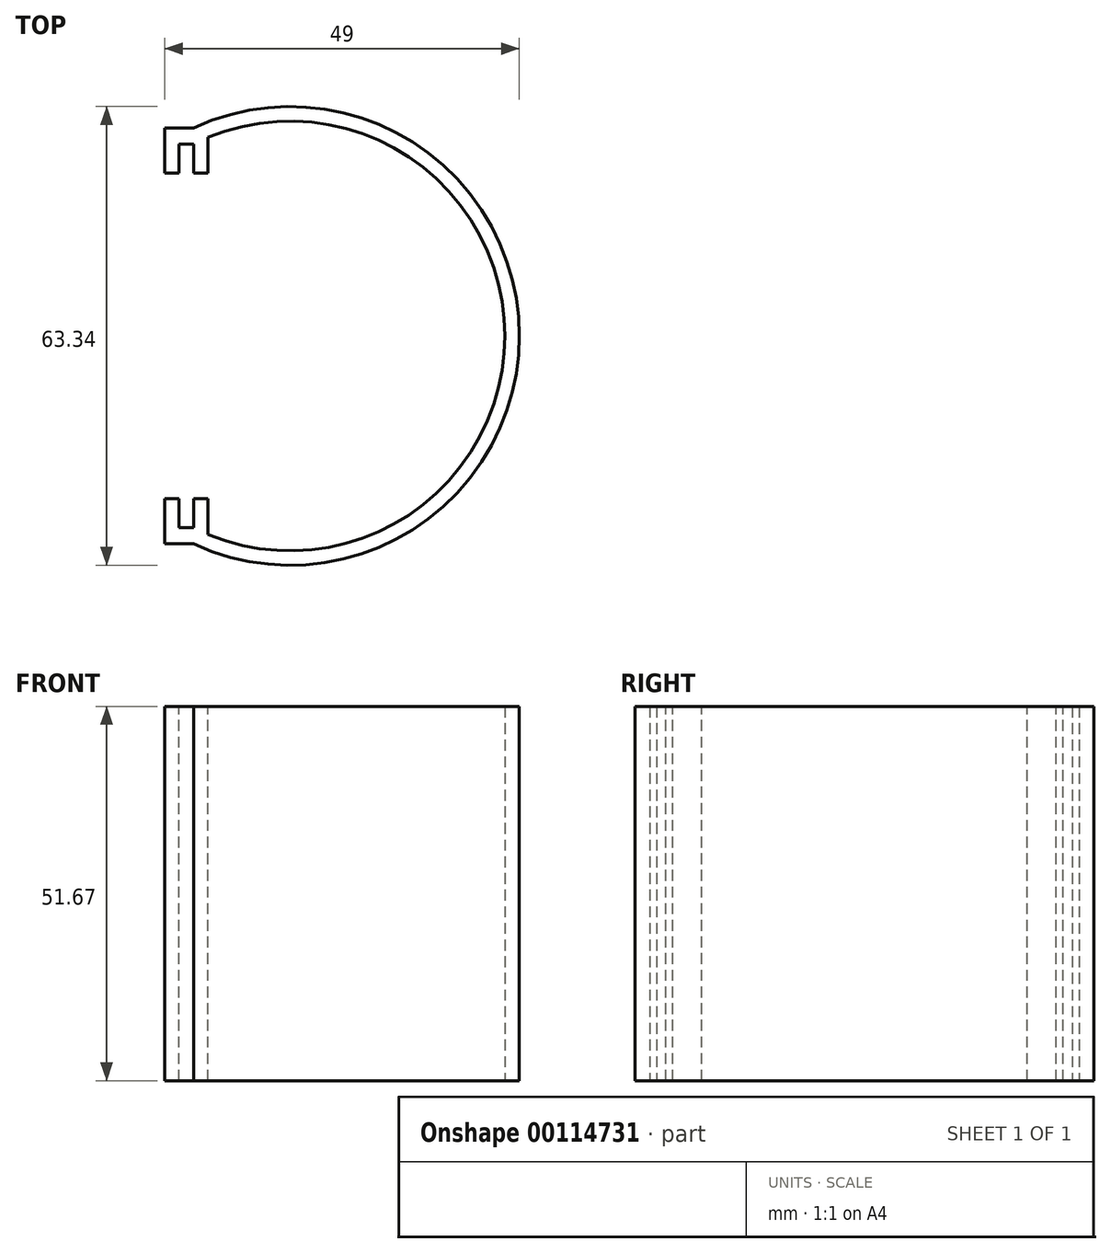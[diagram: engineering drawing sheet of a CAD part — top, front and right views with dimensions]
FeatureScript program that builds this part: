
annotation { "Feature Type Name" : "Feature", "Feature Type Description" : "" }
export const myFeature = defineFeature(function(context is Context, id is Id, definition is map)
    precondition{}
    {
        {
            var Q0;
            Q0=qCreatedBy(makeId("Top.planeOp"),FACE);
            var sketch = newSketch(context, id + "F0", { "sketchPlane" : qUnion([Q0])});
            skArc(sketch, "E0", {"start": v(-13.33, -26.5) * mm, "mid": v(29.67, 0) * mm, "end": v(-13.33, 26.5) * mm});
            skLineSegment(sketch, "E1", {"start": v(-13.33, -28.72) * mm, "end": v(-13.33, -26.5) * mm});
            skPoint(sketch, "E2", {"position": v(-13.33, 26.5) * mm});
            skPoint(sketch, "E3", {"position": v(-13.33, -26.5) * mm});
            skArc(sketch, "E4", {"start": v(-13.33, -28.72) * mm, "mid": v(31.67, 0) * mm, "end": v(-13.33, 28.72) * mm});
            skLineSegment(sketch, "E5.trimOffspring", {"start": v(-13.33, 26.5) * mm, "end": v(-13.33, 28.72) * mm});
            skPoint(sketch, "E6.start.orphan", {"position": v(-13.33, 0) * mm});
            skPoint(sketch, "E7.orphan", {"position": v(-13.33, 36.5) * mm});
            skPoint(sketch, "E8.orphan", {"position": v(-13.33, -36.5) * mm});
            skSolve(sketch);
        }
        {
            var Q0;
            Q0 = qSketchRegion(id + "F0", true);
            extrude(context, id + "F1", {"entities" : qUnion([Q0]), "depth" : 51.67 * mm});
        }
        {
            var Q0;
            Q0=makeQuery(id+"F1.opExtrude","CAP_FACE",FACE,{"disambiguationData":[OSD([sQuery(id+"F0.wireOp",EDGE,"E0"),sQuery(id+"F0.wireOp",EDGE,"E1"),sQuery(id+"F0.wireOp",EDGE,"E4"),sQuery(id+"F0.wireOp",EDGE,"E5.trimOffspring")])],"isStart":false});
            var sketch = newSketch(context, id + "F2", { "sketchPlane" : qUnion([Q0])});
            skLineSegment(sketch, "E9", {"start": v(-11.33, 27.42) * mm, "end": v(-11.33, 22.5) * mm});
            skLineSegment(sketch, "E10", {"start": v(-11.33, 22.5) * mm, "end": v(-13.33, 22.5) * mm});
            skLineSegment(sketch, "E11", {"start": v(-13.33, 22.5) * mm, "end": v(-13.33, 26.5) * mm});
            skLineSegment(sketch, "E12", {"start": v(-13.33, 26.5) * mm, "end": v(-15.33, 26.5) * mm});
            skLineSegment(sketch, "E13", {"start": v(-15.33, 26.5) * mm, "end": v(-15.33, 22.5) * mm});
            skLineSegment(sketch, "E14", {"start": v(-15.33, 22.5) * mm, "end": v(-17.33, 22.5) * mm});
            skLineSegment(sketch, "E15", {"start": v(-17.33, 22.5) * mm, "end": v(-17.33, 26.5) * mm});
            skLineSegment(sketch, "E16", {"start": v(-17.33, 26.5) * mm, "end": v(-17.33, 28.72) * mm});
            skLineSegment(sketch, "E17", {"start": v(-17.33, 28.72) * mm, "end": v(-13.33, 28.72) * mm});
            skSolve(sketch);
        }
        {
            var Q0;
            Q0=makeQuery(id+"F2.imprint","IMPRINT",FACE,{"disambiguationData":[TD([[makeQuery(id+"F2.imprint","IMPRINT",EDGE,{"derivedFrom":sQuery(id+"F2.wireOp",EDGE,"E12")}),-1.0]])]});
            var Q1;
            {var subQ0=sQuery(id+"F2.wireOp",EDGE,"E9");Q1=makeQuery(id+"F2.imprint","IMPRINT",FACE,{"disambiguationData":[TD([[makeQuery(id+"F2.imprint","IMPRINT",EDGE,{"derivedFrom":subQ0}),-1.0]])]});}
            extrude(context, id + "F3", {"entities" : qUnion([Q0, Q1]), "operationType" : NewBodyOperationType.ADD, "oppositeDirection" : true, "depth" : 51.67 * mm});
        }
        {
            var Q0;
            Q0=makeQuery(id+"F1.opExtrude","SWEPT_BODY",BODY,{"disambiguationData":[OSD([sQuery(id+"F0.wireOp",EDGE,"E0"),sQuery(id+"F0.wireOp",EDGE,"E1"),sQuery(id+"F0.wireOp",EDGE,"E4"),sQuery(id+"F0.wireOp",EDGE,"E5.trimOffspring")])]});
            var Q1;
            Q1=qCreatedBy(makeId("Front.planeOp"),FACE);
            mirror(context, id + "F4", {"operationType" : NewBodyOperationType.ADD, "entities" : qUnion([Q0]), "mirrorPlane" : qUnion([Q1])});
        }
        {
            var Q0;
            {var subQ0=sQuery(id+"F0.wireOp",EDGE,"E5.trimOffspring");var subQ1=sQuery(id+"F0.wireOp",EDGE,"E0");var subQ2=makeQuery(id+"F3.boolean.opBoolean","MERGE",FACE,{"derivedFrom":[makeQuery(id+"F1.opExtrude","CAP_FACE",FACE,{"disambiguationData":[OSD([subQ1,sQuery(id+"F0.wireOp",EDGE,"E1"),sQuery(id+"F0.wireOp",EDGE,"E4"),subQ0])],"isStart":false}),makeQuery(id+"F3.opExtrude","CAP_FACE",FACE,{"disambiguationData":[OSD([subQ1,sQuery(id+"F2.wireOp",EDGE,"E9"),sQuery(id+"F2.wireOp",EDGE,"E10"),sQuery(id+"F2.wireOp",EDGE,"E11")])],"isStart":true}),makeQuery(id+"F3.opExtrude","CAP_FACE",FACE,{"disambiguationData":[OSD([subQ0,sQuery(id+"F2.wireOp",EDGE,"E12"),sQuery(id+"F2.wireOp",EDGE,"E13"),sQuery(id+"F2.wireOp",EDGE,"E14"),sQuery(id+"F2.wireOp",EDGE,"E15"),sQuery(id+"F2.wireOp",EDGE,"E16"),sQuery(id+"F2.wireOp",EDGE,"E17")])],"isStart":true})]});Q0=makeQuery(id+"F4.boolean.opBoolean","MERGE",FACE,{"derivedFrom":[subQ2,makeQuery(id+"F4.opPattern","COPY",FACE,{"derivedFrom":subQ2,"instanceName":"1"})]});}
            cPlane(context, id + "F5", {"entities" : qUnion([Q0]), "cplaneType" : CPlaneType.OFFSET, "offset" : 9.17 * mm, "width" : 150 * mm, "height" : 150 * mm});
        }
    });
